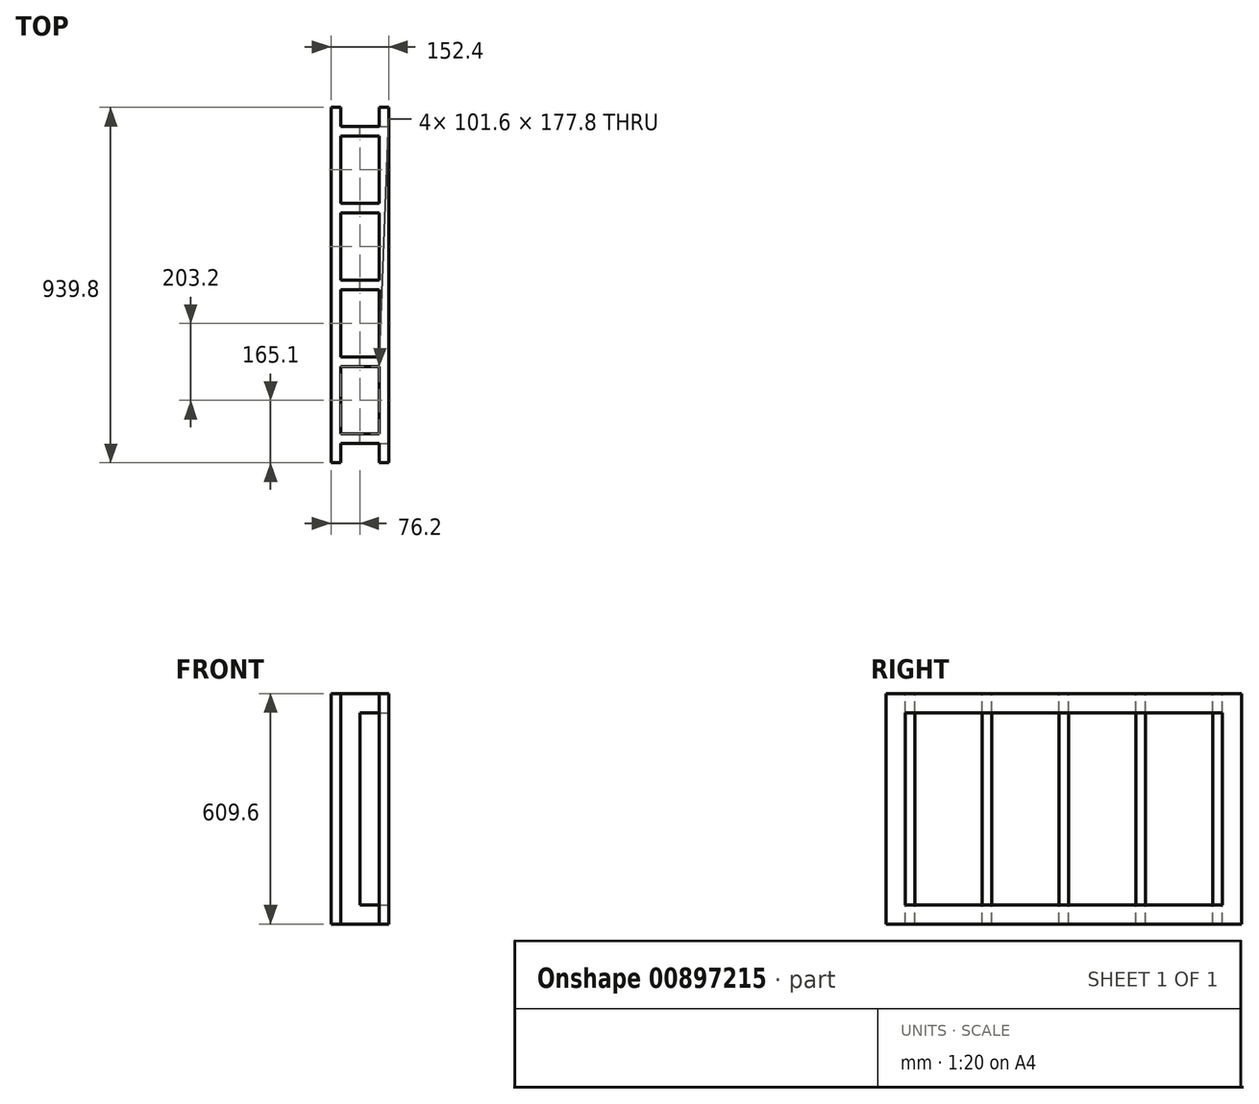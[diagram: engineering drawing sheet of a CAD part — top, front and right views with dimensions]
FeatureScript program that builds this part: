
annotation { "Feature Type Name" : "Feature", "Feature Type Description" : "" }
export const myFeature = defineFeature(function(context is Context, id is Id, definition is map)
    precondition{}
    {
        {
            var Q0;
            Q0=qCreatedBy(makeId("Top.planeOp"),FACE);
            var sketch = newSketch(context, id + "F0", { "sketchPlane" : qUnion([Q0])});
            skLineSegment(sketch, "E0.top", {"start": v(0, 838.2) * mm, "end": v(152.4, 838.2) * mm});
            skLineSegment(sketch, "E0.left", {"start": v(0, 419.1) * mm, "end": v(0, 838.2) * mm});
            skLineSegment(sketch, "E0.right", {"start": v(152.4, 419.1) * mm, "end": v(152.4, 431.8) * mm});
            skLineSegment(sketch, "E1", {"start": v(25.4, 812.8) * mm, "end": v(152.4, 812.8) * mm});
            skLineSegment(sketch, "E2", {"start": v(0, 419.1) * mm, "end": v(416.46, 419.1) * mm, "construction": true});
            skLineSegment(sketch, "E3", {"start": v(25.4, 812.8) * mm, "end": v(25.4, 635) * mm});
            skLineSegment(sketch, "E4", {"start": v(25.4, 431.8) * mm, "end": v(152.4, 431.8) * mm});
            skPoint(sketch, "E0.bottom.start.orphan", {"position": v(0, 0) * mm});
            skLineSegment(sketch, "E5.trimOffspring", {"start": v(152.4, 812.8) * mm, "end": v(152.4, 838.2) * mm});
            skLineSegment(sketch, "E6.MirrorCS", {"start": v(152.4, 25.4) * mm, "end": v(152.4, 0) * mm});
            skLineSegment(sketch, "E7.MirrorCS", {"start": v(152.4, 419.1) * mm, "end": v(152.4, 406.4) * mm});
            skLineSegment(sketch, "E8.MirrorCS", {"start": v(25.4, 25.4) * mm, "end": v(152.4, 25.4) * mm});
            skLineSegment(sketch, "E9.MirrorCS", {"start": v(0, 0) * mm, "end": v(152.4, 0) * mm});
            skLineSegment(sketch, "E10.MirrorCS", {"start": v(25.4, 406.4) * mm, "end": v(152.4, 406.4) * mm});
            skLineSegment(sketch, "E11.MirrorCS", {"start": v(25.4, 25.4) * mm, "end": v(25.4, 203.2) * mm});
            skLineSegment(sketch, "E12.MirrorCS", {"start": v(0, 419.1) * mm, "end": v(0, 0) * mm});
            skPoint(sketch, "E13.orphan", {"position": v(25.4, 419.1) * mm});
            skLineSegment(sketch, "E14.0.1.0", {"start": v(25.4, 635) * mm, "end": v(152.4, 635) * mm});
            skLineSegment(sketch, "E14.0.1.1", {"start": v(152.4, 622.3) * mm, "end": v(152.4, 635) * mm});
            skLineSegment(sketch, "E14.0.1.2", {"start": v(152.4, 622.3) * mm, "end": v(152.4, 609.6) * mm});
            skLineSegment(sketch, "E14.0.1.3", {"start": v(25.4, 609.6) * mm, "end": v(152.4, 609.6) * mm});
            skLineSegment(sketch, "E14.direction1", {"start": v(25.4, 431.8) * mm, "end": v(50.8, 431.8) * mm, "construction": true});
            skLineSegment(sketch, "E14.direction2", {"start": v(25.4, 431.8) * mm, "end": v(25.4, 609.6) * mm, "construction": true});
            skLineSegment(sketch, "E15.trimOffspring", {"start": v(25.4, 609.6) * mm, "end": v(25.4, 431.8) * mm});
            skLineSegment(sketch, "E16.MirrorCS", {"start": v(25.4, 203.2) * mm, "end": v(152.4, 203.2) * mm});
            skLineSegment(sketch, "E17.MirrorCS", {"start": v(25.4, 228.6) * mm, "end": v(152.4, 228.6) * mm});
            skLineSegment(sketch, "E18.MirrorCS", {"start": v(152.4, 215.9) * mm, "end": v(152.4, 203.2) * mm});
            skLineSegment(sketch, "E19.MirrorCS", {"start": v(152.4, 215.9) * mm, "end": v(152.4, 228.6) * mm});
            skLineSegment(sketch, "E20.trimOffspring", {"start": v(25.4, 228.6) * mm, "end": v(25.4, 406.4) * mm});
            skSolve(sketch);
        }
        {
            var Q0;
            Q0=qSketchRegion(id+"F0",true);
            extrude(context, id + "F1", {"entities" : qUnion([Q0]), "oppositeDirection" : true, "depth" : 609.6 * mm, "offsetDistance" : 25.4 * mm});
        }
        {
            var Q0;
            Q0=makeQuery(id+"F0.imprint","IMPRINT",FACE,{"disambiguationData":[TD([[makeQuery(id+"F0.imprint","IMPRINT",EDGE,{"derivedFrom":sQuery(id+"F0.wireOp",EDGE,"E0.top")}),-1.0]])]});
            var sketch = newSketch(context, id + "F2", { "sketchPlane" : qUnion([Q0])});
            skLineSegment(sketch, "E21.bottom", {"start": v(0, 838.2) * mm, "end": v(25.4, 838.2) * mm});
            skLineSegment(sketch, "E21.top", {"start": v(0, 889) * mm, "end": v(25.4, 889) * mm});
            skLineSegment(sketch, "E21.left", {"start": v(0, 838.2) * mm, "end": v(0, 889) * mm});
            skLineSegment(sketch, "E21.right", {"start": v(25.4, 838.2) * mm, "end": v(25.4, 889) * mm});
            skLineSegment(sketch, "E22.MirrorCS", {"start": v(0, -50.8) * mm, "end": v(25.4, -50.8) * mm});
            skLineSegment(sketch, "E23.MirrorCS", {"start": v(0, 0) * mm, "end": v(0, -50.8) * mm});
            skLineSegment(sketch, "E24.MirrorCS", {"start": v(0, 0) * mm, "end": v(25.4, 0) * mm});
            skLineSegment(sketch, "E25.MirrorCS", {"start": v(25.4, 0) * mm, "end": v(25.4, -50.8) * mm});
            skLineSegment(sketch, "E26.bottom", {"start": v(152.4, 838.2) * mm, "end": v(127, 838.2) * mm});
            skLineSegment(sketch, "E26.top", {"start": v(152.4, 0) * mm, "end": v(127, 0) * mm});
            skLineSegment(sketch, "E26.left", {"start": v(152.4, 838.2) * mm, "end": v(152.4, 0) * mm});
            skLineSegment(sketch, "E26.right", {"start": v(127, 838.2) * mm, "end": v(127, 0) * mm});
            skLineSegment(sketch, "E27.top", {"start": v(152.4, 889) * mm, "end": v(127, 889) * mm});
            skLineSegment(sketch, "E27.left", {"start": v(152.4, 838.2) * mm, "end": v(152.4, 889) * mm});
            skLineSegment(sketch, "E27.right", {"start": v(127, 838.2) * mm, "end": v(127, 889) * mm});
            skLineSegment(sketch, "E28.MirrorCS", {"start": v(152.4, 0) * mm, "end": v(152.4, -50.8) * mm});
            skLineSegment(sketch, "E29.MirrorCS", {"start": v(127, 0) * mm, "end": v(127, -50.8) * mm});
            skLineSegment(sketch, "E30.MirrorCS", {"start": v(152.4, -50.8) * mm, "end": v(127, -50.8) * mm});
            skSolve(sketch);
        }
        {
            var Q0;
            Q0=qSketchRegion(id+"F2",true);
            extrude(context, id + "F3", {"entities" : qUnion([Q0]), "operationType" : NewBodyOperationType.ADD, "oppositeDirection" : true, "depth" : 609.6 * mm, "offsetDistance" : 25.4 * mm});
        }
        {
            var Q0;
            Q0=makeQuery(id+"F3.boolean.opBoolean","MERGE",FACE,{"derivedFrom":[makeQuery(id+"F1.opExtrude","SWEPT_FACE",FACE,{"disambiguationData":[OSD([sQuery(id+"F0.wireOp",EDGE,"E0.right"),sQuery(id+"F0.wireOp",EDGE,"E7.MirrorCS")])]}),makeQuery(id+"F1.opExtrude","SWEPT_FACE",FACE,{"disambiguationData":[OSD([sQuery(id+"F0.wireOp",EDGE,"E5.trimOffspring")])]}),makeQuery(id+"F1.opExtrude","SWEPT_FACE",FACE,{"disambiguationData":[OSD([sQuery(id+"F0.wireOp",EDGE,"E6.MirrorCS")])]}),makeQuery(id+"F1.opExtrude","SWEPT_FACE",FACE,{"disambiguationData":[OSD([sQuery(id+"F0.wireOp",EDGE,"E14.0.1.1"),sQuery(id+"F0.wireOp",EDGE,"E14.0.1.2")])]}),makeQuery(id+"F1.opExtrude","SWEPT_FACE",FACE,{"disambiguationData":[OSD([sQuery(id+"F0.wireOp",EDGE,"E18.MirrorCS"),sQuery(id+"F0.wireOp",EDGE,"E19.MirrorCS")])]}),makeQuery(id+"F3.opExtrude","SWEPT_FACE",FACE,{"disambiguationData":[OSD([sQuery(id+"F2.wireOp",EDGE,"E26.left"),sQuery(id+"F2.wireOp",EDGE,"E27.left"),sQuery(id+"F2.wireOp",EDGE,"E28.MirrorCS")])]})]});
            var sketch = newSketch(context, id + "F4", { "sketchPlane" : qUnion([Q0])});
            skLineSegment(sketch, "E31.bottom", {"start": v(-50.8, 0) * mm, "end": v(889, 0) * mm, "construction": true});
            skLineSegment(sketch, "E31.top", {"start": v(-50.8, -609.6) * mm, "end": v(889, -609.6) * mm, "construction": true});
            skLineSegment(sketch, "E31.left", {"start": v(-50.8, 0) * mm, "end": v(-50.8, -609.6) * mm, "construction": true});
            skLineSegment(sketch, "E31.right", {"start": v(889, 0) * mm, "end": v(889, -609.6) * mm, "construction": true});
            skLineSegment(sketch, "E32.0", {"start": v(0, -50.8) * mm, "end": v(838.2, -50.8) * mm});
            skLineSegment(sketch, "E32.1", {"start": v(0, -50.8) * mm, "end": v(0, -558.8) * mm});
            skLineSegment(sketch, "E32.2", {"start": v(0, -558.8) * mm, "end": v(838.2, -558.8) * mm});
            skLineSegment(sketch, "E32.3", {"start": v(838.2, -50.8) * mm, "end": v(838.2, -558.8) * mm});
            skSolve(sketch);
        }
        {
            var Q0;
            Q0 = qSketchRegion(id + "F4", true);
            extrude(context, id + "F5", {"entities" : qUnion([Q0]), "operationType" : NewBodyOperationType.REMOVE, "oppositeDirection" : true, "depth" : 76.2 * mm, "offsetDistance" : 25.4 * mm});
        }
    });
